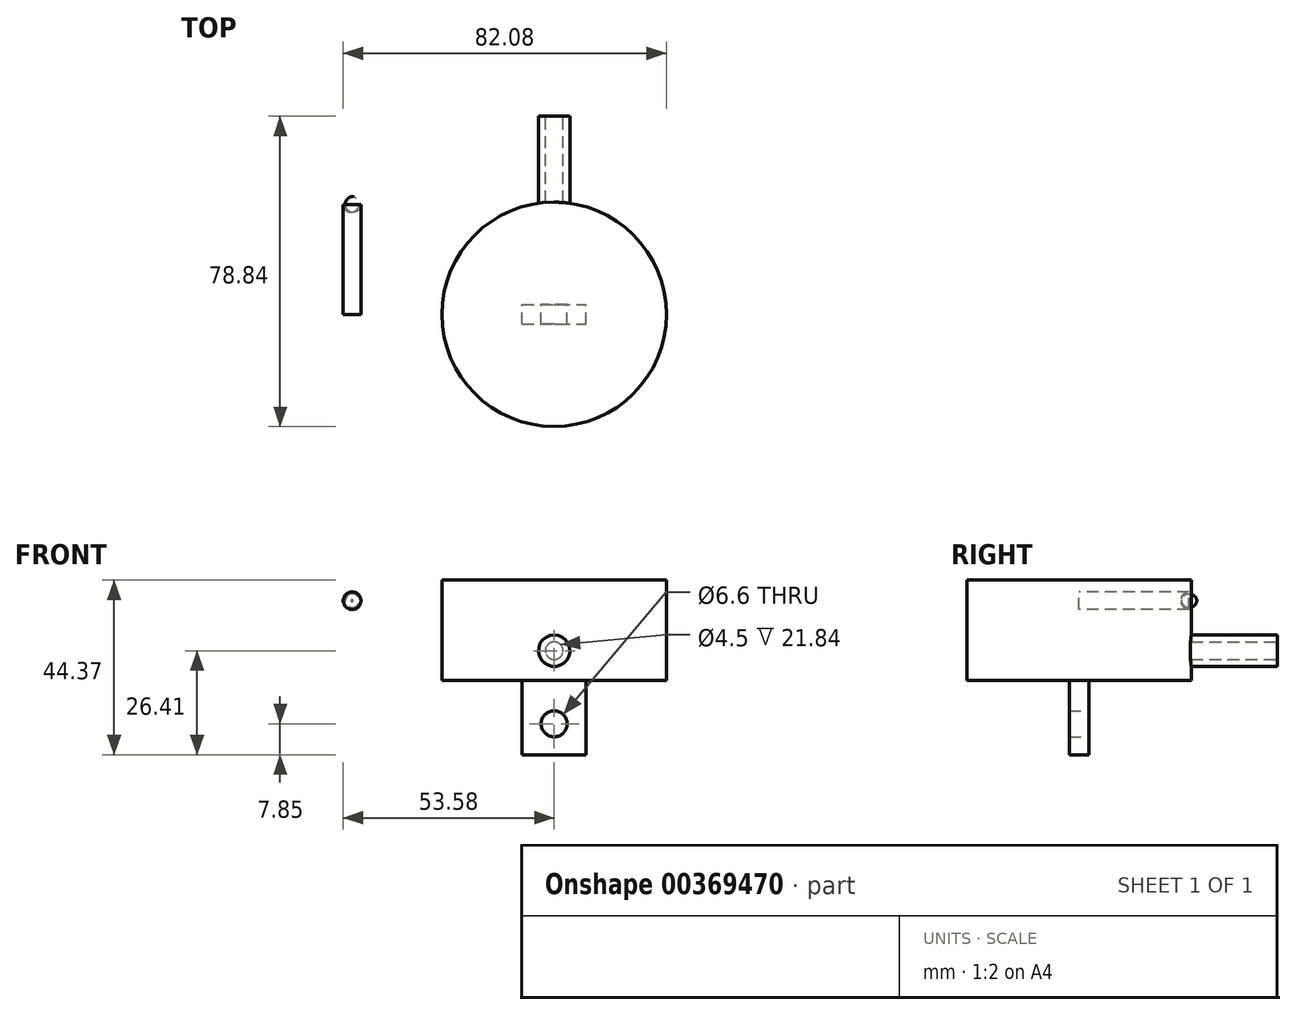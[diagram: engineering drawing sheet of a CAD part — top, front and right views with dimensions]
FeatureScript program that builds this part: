
annotation { "Feature Type Name" : "Feature", "Feature Type Description" : "" }
export const myFeature = defineFeature(function(context is Context, id is Id, definition is map)
    precondition{}
    {
        {
            var Q0;
            Q0=qCreatedBy(makeId("Top.planeOp"),FACE);
            var sketch = newSketch(context, id + "F0", { "sketchPlane" : qUnion([Q0])});
            skCircle(sketch, "E0", {"center": v(0, 0) * mm, "radius": 28.5 * mm});
            skSolve(sketch);
        }
        {
            var Q0;
            Q0=makeQuery(id+"F0.imprint","IMPRINT",FACE,{"disambiguationData":[TD([[makeQuery(id+"F0.imprint","IMPRINT",EDGE,{"derivedFrom":sQuery(id+"F0.wireOp",EDGE,"E0")}),1.0]])]});
            extrude(context, id + "F1", {"entities" : qUnion([Q0]), "depth" : 25.52 * mm});
        }
        {
            var Q0;
            Q0=makeQuery(id+"F1.opExtrude","CAP_FACE",FACE,{"disambiguationData":[OSD([sQuery(id+"F0.wireOp",EDGE,"E0")])],"isStart":true});
            var sketch = newSketch(context, id + "F2", { "sketchPlane" : qUnion([Q0])});
            skLineSegment(sketch, "E1.bottom", {"start": v(-8.12, 2.5) * mm, "end": v(8.12, 2.5) * mm});
            skLineSegment(sketch, "E1.top", {"start": v(-8.12, -2.5) * mm, "end": v(8.12, -2.5) * mm});
            skLineSegment(sketch, "E1.left", {"start": v(-8.12, 2.5) * mm, "end": v(-8.12, -2.5) * mm});
            skLineSegment(sketch, "E1.right", {"start": v(8.12, 2.5) * mm, "end": v(8.12, -2.5) * mm});
            skPoint(sketch, "E1.middle", {"position": v(0, 0) * mm});
            skSolve(sketch);
        }
        {
            var Q0;
            Q0=makeQuery(id+"F2.imprint","IMPRINT",FACE,{"disambiguationData":[TD([[makeQuery(id+"F2.imprint","IMPRINT",EDGE,{"derivedFrom":sQuery(id+"F2.wireOp",EDGE,"E1.bottom")}),-1.0]])]});
            extrude(context, id + "F3", {"entities" : qUnion([Q0]), "operationType" : NewBodyOperationType.ADD, "depth" : 18.85 * mm});
        }
        {
            var Q0;
            Q0=makeQuery(id+"F3.opExtrude","SWEPT_FACE",FACE,{"disambiguationData":[OSD([sQuery(id+"F2.wireOp",EDGE,"E1.top")])]});
            var sketch = newSketch(context, id + "F4", { "sketchPlane" : qUnion([Q0])});
            skCircle(sketch, "E2", {"center": v(0, -11) * mm, "radius": 3.3 * mm});
            skSolve(sketch);
        }
        {
            var Q0;
            Q0=makeQuery(id+"F4.imprint","IMPRINT",FACE,{"disambiguationData":[TD([[makeQuery(id+"F4.imprint","IMPRINT",EDGE,{"derivedFrom":sQuery(id+"F4.wireOp",EDGE,"E2")}),1.0]])]});
            var Q1;
            Q1=makeQuery(id+"F3.opExtrude","SWEPT_FACE",FACE,{"disambiguationData":[OSD([sQuery(id+"F2.wireOp",EDGE,"E1.bottom")])]});
            extrude(context, id + "F5", {"entities" : qUnion([Q0]), "operationType" : NewBodyOperationType.REMOVE, "endBound" : BoundingType.UP_TO_SURFACE, "oppositeDirection" : true, "endBoundEntityFace" : qUnion([Q1]), "depth" : 25 * mm});
        }
        {
            var Q0;
            Q0=makeQuery(id+"F1.opExtrude","CAP_FACE",FACE,{"disambiguationData":[OSD([sQuery(id+"F0.wireOp",EDGE,"E0")])],"isStart":true});
            var sketch = newSketch(context, id + "F6", { "sketchPlane" : qUnion([Q0])});
            skPoint(sketch, "E3", {"position": v(0, -28.5) * mm});
            skPoint(sketch, "E3.positionSnap0", {"position": v(0, -2.5) * mm});
            skSolve(sketch);
        }
        {
            var Q0;
            Q0=qCreatedBy(makeId("Front.planeOp"),FACE);
            var Q1;
            Q1=sQuery(id+"F6.wireOp",VERTEX,"E3");
            cPlane(context, id + "F7", {"entities" : qUnion([Q0, Q1]), "cplaneType" : CPlaneType.PLANE_POINT, "offset" : 25 * mm, "width" : 150 * mm, "height" : 150 * mm});
        }
        {
            var Q0;
            Q0=qCreatedBy(id+"F7.planeOp",FACE);
            var sketch = newSketch(context, id + "F8", { "sketchPlane" : qUnion([Q0])});
            skCircle(sketch, "E4", {"center": v(0, 7.56) * mm, "radius": 3.98 * mm});
            skSolve(sketch);
        }
        {
            var Q0;
            Q0=makeQuery(id+"F8.imprint","IMPRINT",FACE,{"disambiguationData":[TD([[makeQuery(id+"F8.imprint","IMPRINT",EDGE,{"derivedFrom":sQuery(id+"F8.wireOp",EDGE,"E4")}),1.0]])]});
            var Q1;
            Q1=makeQuery(id+"F1.opExtrude","SWEPT_BODY",BODY,{"disambiguationData":[OSD([sQuery(id+"F0.wireOp",EDGE,"E0")])]});
            extrude(context, id + "F9", {"entities" : qUnion([Q0]), "operationType" : NewBodyOperationType.ADD, "endBoundEntityBody" : qUnion([Q1]), "depth" : 2 * mm});
        }
        {
            var Q0;
            Q0=makeQuery(id+"F8.imprint","IMPRINT",FACE,{"disambiguationData":[TD([[makeQuery(id+"F8.imprint","IMPRINT",EDGE,{"derivedFrom":sQuery(id+"F8.wireOp",EDGE,"E4")}),1.0]])]});
            extrude(context, id + "F10", {"entities" : qUnion([Q0]), "operationType" : NewBodyOperationType.ADD, "oppositeDirection" : true, "depth" : 21.84 * mm});
        }
        {
            var Q0;
            Q0=makeQuery(id+"F10.opExtrude","CAP_FACE",FACE,{"disambiguationData":[OSD([sQuery(id+"F8.wireOp",EDGE,"E4")])],"isStart":false});
            var sketch = newSketch(context, id + "F11", { "sketchPlane" : qUnion([Q0])});
            skCircle(sketch, "E5", {"center": v(0, 7.56) * mm, "radius": 2.25 * mm});
            skSolve(sketch);
        }
        {
            var Q0;
            Q0=makeQuery(id+"F11.imprint","IMPRINT",FACE,{"disambiguationData":[TD([[makeQuery(id+"F11.imprint","IMPRINT",EDGE,{"derivedFrom":sQuery(id+"F11.wireOp",EDGE,"E5")}),1.0]])]});
            var Q1;
            Q1=qCreatedBy(id+"F7.planeOp",FACE);
            extrude(context, id + "F12", {"entities" : qUnion([Q0]), "operationType" : NewBodyOperationType.REMOVE, "endBound" : BoundingType.UP_TO_SURFACE, "oppositeDirection" : true, "endBoundEntityFace" : qUnion([Q1]), "depth" : 25 * mm});
        }
        {
            var Q0;
            Q0=qCreatedBy(makeId("Front.planeOp"),FACE);
            var sketch = newSketch(context, id + "F13", { "sketchPlane" : qUnion([Q0])});
            skCircle(sketch, "E6", {"center": v(-51.33, 20.27) * mm, "radius": 2.25 * mm});
            skSolve(sketch);
        }
        {
            var Q0;
            Q0=makeQuery(id+"F13.imprint","IMPRINT",FACE,{"disambiguationData":[TD([[makeQuery(id+"F13.imprint","IMPRINT",EDGE,{"derivedFrom":sQuery(id+"F13.wireOp",EDGE,"E6")}),1.0]])]});
            extrude(context, id + "F14", {"entities" : qUnion([Q0]), "oppositeDirection" : true, "depth" : 29.94 * mm});
        }
        {
            var Q0;
            Q0=makeQuery(id+"F14.opExtrude","CAP_EDGE",EDGE,{"disambiguationData":[OSD([sQuery(id+"F13.wireOp",EDGE,"E6")])],"isStart":false});
            fillet(context, id + "F15", {"entities" : qUnion([Q0]), "radius" : 2 * mm, "tangentPropagation" : true, "allowEdgeOverflow" : false});
        }
    });
